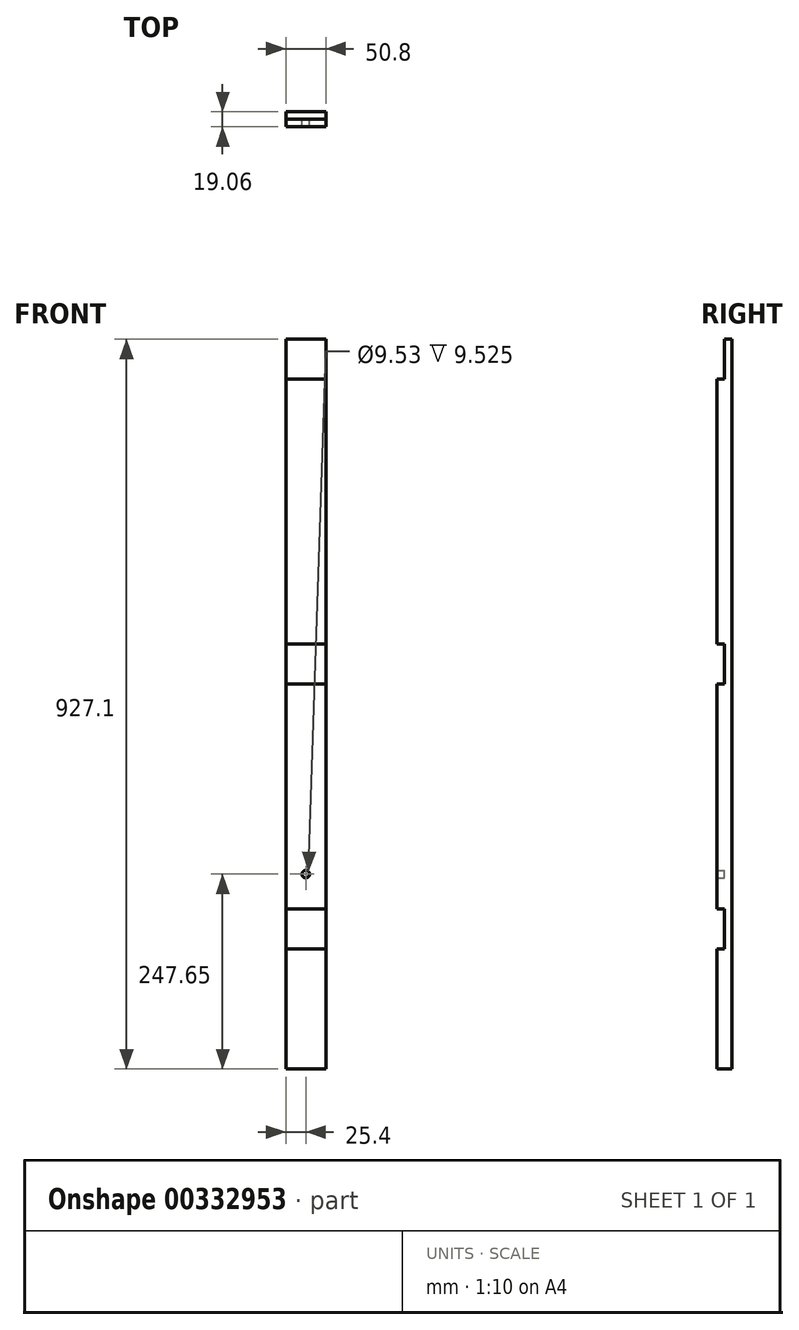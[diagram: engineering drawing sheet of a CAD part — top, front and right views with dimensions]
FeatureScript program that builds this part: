
annotation { "Feature Type Name" : "Feature", "Feature Type Description" : "" }
export const myFeature = defineFeature(function(context is Context, id is Id, definition is map)
    precondition{}
    {
        {
            var Q0;
            Q0=qCreatedBy(makeId("Top.planeOp"),FACE);
            var sketch = newSketch(context, id + "F0", { "sketchPlane" : qUnion([Q0])});
            skLineSegment(sketch, "E0.bottom", {"start": v(25.4, 9.53) * mm, "end": v(-25.4, 9.53) * mm});
            skLineSegment(sketch, "E0.top", {"start": v(25.4, -9.53) * mm, "end": v(-25.4, -9.53) * mm});
            skLineSegment(sketch, "E0.left", {"start": v(25.4, 9.53) * mm, "end": v(25.4, -9.52) * mm});
            skLineSegment(sketch, "E0.right", {"start": v(-25.4, 9.53) * mm, "end": v(-25.4, -9.53) * mm});
            skPoint(sketch, "E0.middle", {"position": v(0, 0) * mm});
            skSolve(sketch);
        }
        {
            var Q0;
            Q0=makeQuery(id+"F0.imprint","IMPRINT",FACE,{"disambiguationData":[TD([[makeQuery(id+"F0.imprint","IMPRINT",EDGE,{"derivedFrom":sQuery(id+"F0.wireOp",EDGE,"E0.bottom")}),1.0]])]});
            var Q1;
            Q1=qSketchRegion(id+"F2",true);
            extrude(context, id + "F1", {"entities" : qUnion([Q0, Q1]), "depth" : 927.1 * mm});
        }
        {
            var Q0;
            Q0=qCreatedBy(makeId("Front.planeOp"),FACE);
            var sketch = newSketch(context, id + "F2", { "sketchPlane" : qUnion([Q0])});
            skLineSegment(sketch, "E1.bottom", {"start": v(-38.77, 152.4) * mm, "end": v(83.66, 152.4) * mm});
            skLineSegment(sketch, "E1.top", {"start": v(-38.77, 203.2) * mm, "end": v(83.66, 203.2) * mm});
            skLineSegment(sketch, "E1.left", {"start": v(-38.77, 152.4) * mm, "end": v(-38.77, 203.2) * mm});
            skLineSegment(sketch, "E1.right", {"start": v(83.66, 152.4) * mm, "end": v(83.66, 203.2) * mm});
            skLineSegment(sketch, "E2.bottom", {"start": v(-210.36, 876.3) * mm, "end": v(132.8, 876.3) * mm});
            skLineSegment(sketch, "E2.top", {"start": v(-210.36, 927.1) * mm, "end": v(132.8, 927.1) * mm});
            skLineSegment(sketch, "E2.left", {"start": v(-210.36, 876.3) * mm, "end": v(-210.36, 927.1) * mm});
            skLineSegment(sketch, "E2.right", {"start": v(132.8, 876.3) * mm, "end": v(132.8, 927.1) * mm});
            skLineSegment(sketch, "E3.bottom", {"start": v(-179.92, 539.75) * mm, "end": v(84.62, 539.75) * mm});
            skLineSegment(sketch, "E3.top", {"start": v(-179.92, 488.95) * mm, "end": v(84.62, 488.95) * mm});
            skLineSegment(sketch, "E3.left", {"start": v(-179.92, 539.75) * mm, "end": v(-179.92, 488.95) * mm});
            skLineSegment(sketch, "E3.right", {"start": v(84.62, 539.75) * mm, "end": v(84.62, 488.95) * mm});
            skSolve(sketch);
        }
        {
            var Q0;
            Q0=qSketchRegion(id+"F2",true);
            extrude(context, id + "F3", {"entities" : qUnion([Q0]), "operationType" : NewBodyOperationType.REMOVE, "depth" : 25.4 * mm});
        }
        {
            var Q0;
            Q0=qCreatedBy(makeId("Front.planeOp"),FACE);
            var sketch = newSketch(context, id + "F4", { "sketchPlane" : qUnion([Q0])});
            skCircle(sketch, "E4", {"center": v(0, 247.65) * mm, "radius": 4.76 * mm});
            skSolve(sketch);
        }
        {
            var Q0;
            Q0=qSketchRegion(id+"F4",true);
            extrude(context, id + "F5", {"entities" : qUnion([Q0]), "operationType" : NewBodyOperationType.REMOVE, "depth" : 25.4 * mm});
        }
    });
